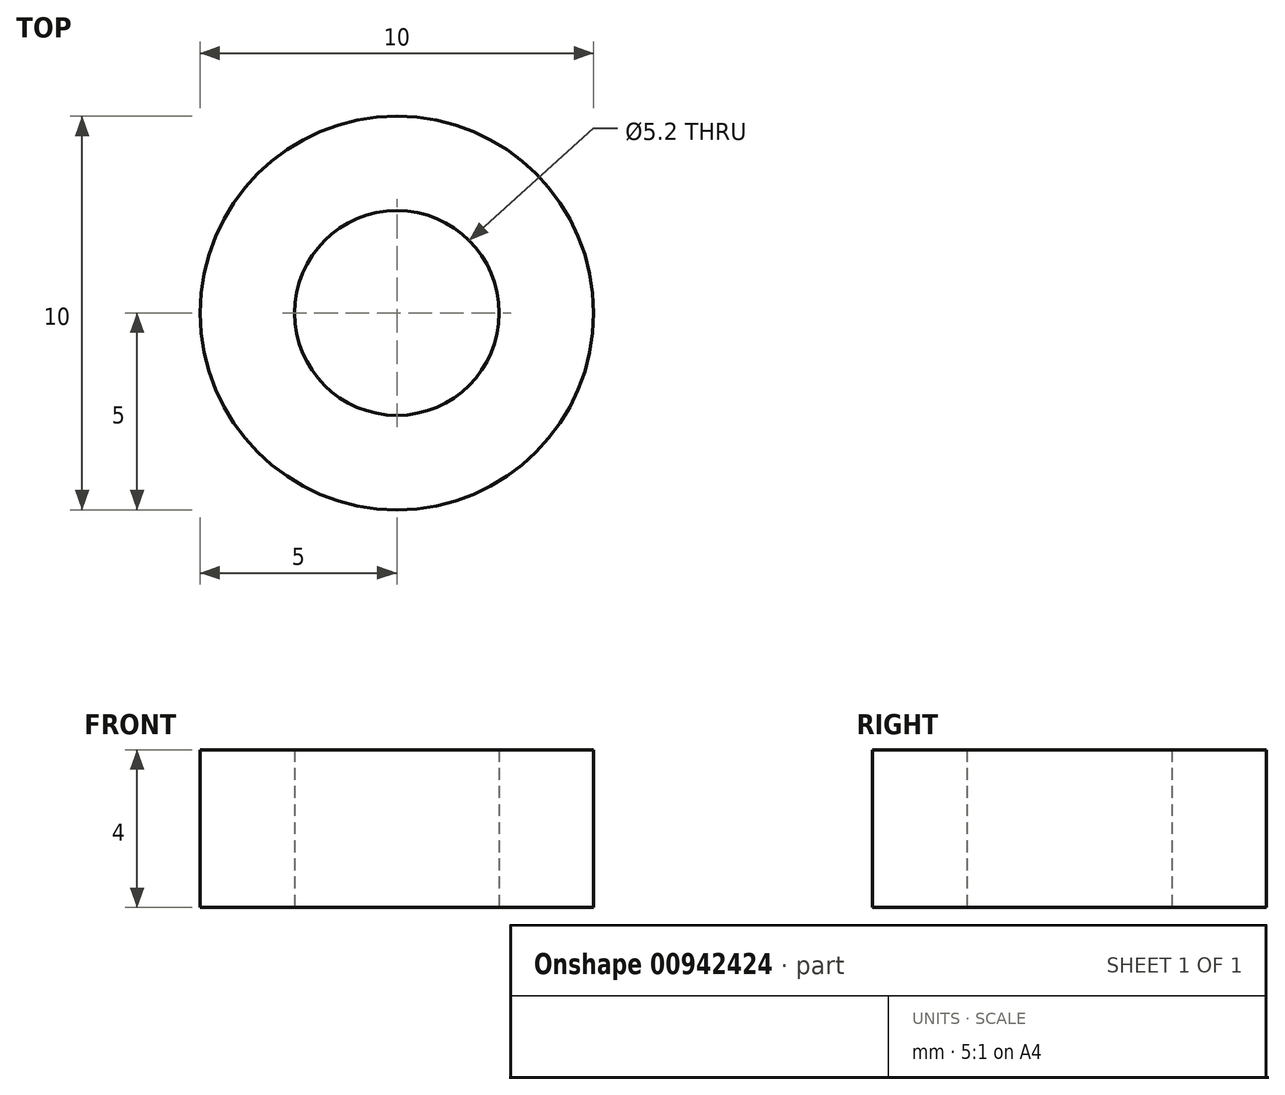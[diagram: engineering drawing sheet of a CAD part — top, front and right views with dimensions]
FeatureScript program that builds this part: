
annotation { "Feature Type Name" : "Feature", "Feature Type Description" : "" }
export const myFeature = defineFeature(function(context is Context, id is Id, definition is map)
    precondition{}
    {
        {
            var Q0;
            Q0=qCreatedBy(makeId("Front.planeOp"),FACE);
            var sketch = newSketch(context, id + "F0", { "sketchPlane" : qUnion([Q0])});
            skLineSegment(sketch, "E0", {"start": v(9.37, 10) * mm, "end": v(9.37, 25) * mm});
            skLineSegment(sketch, "E1", {"start": v(9.37, 25) * mm, "end": v(-30.63, 25) * mm});
            skLineSegment(sketch, "E2", {"start": v(-30.63, 25) * mm, "end": v(-30.63, -25) * mm});
            skLineSegment(sketch, "E3", {"start": v(9.37, -25) * mm, "end": v(9.37, 0) * mm});
            skLineSegment(sketch, "E4", {"start": v(-30.63, -25) * mm, "end": v(9.37, -25) * mm});
            skLineSegment(sketch, "E5", {"start": v(9.37, 10) * mm, "end": v(-10.63, 10) * mm});
            skLineSegment(sketch, "E6", {"start": v(-10.63, 10) * mm, "end": v(-10.63, 0) * mm});
            skLineSegment(sketch, "E7", {"start": v(-10.63, 0) * mm, "end": v(9.37, 0) * mm});
            skLineSegment(sketch, "E8.bottom", {"start": v(-4.1, -6) * mm, "end": v(4.1, -6) * mm});
            skLineSegment(sketch, "E8.top", {"start": v(-4.1, -9.2) * mm, "end": v(4.1, -9.2) * mm});
            skLineSegment(sketch, "E8.left", {"start": v(-4.1, -6) * mm, "end": v(-4.1, -9.2) * mm});
            skLineSegment(sketch, "E8.right", {"start": v(4.1, -6) * mm, "end": v(4.1, -9.2) * mm});
            skFitSpline(sketch, "E9", {"points": [v(-25, 25) * mm, v(-21.25, -15.4) * mm, v(9.37, -19.87) * mm], "startDerivative": vector(2.03, -83.34) * mm, "endDerivative": vector(87.72, 0.68) * mm});
            skSolve(sketch);
        }
        {
            var Q0;
            Q0=qSketchRegion(id+"F0",true);
            extrude(context, id + "F1", {"entities" : qUnion([Q0]), "depth" : 25 * mm, "offsetDistance" : 25 * mm});
        }
        {
            var Q0;
            Q0=makeQuery(id+"F1.opExtrude","SWEPT_FACE",FACE,{"disambiguationData":[OSD([sQuery(id+"F0.wireOp",EDGE,"E1")])]});
            var sketch = newSketch(context, id + "F2", { "sketchPlane" : qUnion([Q0])});
            skCircle(sketch, "E10", {"center": v(-17.63, -12.5) * mm, "radius": 3 * mm});
            skPoint(sketch, "E10.centerSnap0", {"position": v(-10.63, 0) * mm});
            skPoint(sketch, "E10.centerSnap1", {"position": v(-30.63, -12.5) * mm});
            skSolve(sketch);
        }
        {
            var Q0;
            Q0=makeQuery(id+"F2.imprint","IMPRINT",FACE,{"disambiguationData":[TD([[makeQuery(id+"F2.imprint","IMPRINT",EDGE,{"derivedFrom":sQuery(id+"F2.wireOp",EDGE,"E10")}),1.0]])]});
            extrude(context, id + "F3", {"entities" : qUnion([Q0]), "operationType" : NewBodyOperationType.REMOVE, "oppositeDirection" : true, "depth" : 56.7 * mm, "offsetDistance" : 25 * mm});
        }
        {
            var Q0;
            Q0=makeQuery(id+"F1.opExtrude","SWEPT_FACE",FACE,{"disambiguationData":[OSD([sQuery(id+"F0.wireOp",EDGE,"E4")])]});
            var sketch = newSketch(context, id + "F4", { "sketchPlane" : qUnion([Q0])});
            skLineSegment(sketch, "E11", {"start": v(23.4, 12.5) * mm, "end": v(-73.54, 12.5) * mm, "construction": true});
            skLineSegment(sketch, "E12.0", {"start": v(-10.63, 25) * mm, "end": v(-10.63, 0) * mm, "construction": true});
            skCircle(sketch, "E13", {"center": v(0, 12.5) * mm, "radius": 2.6 * mm});
            skSolve(sketch);
        }
        {
            var Q0;
            Q0=makeQuery(id+"F4.imprint","IMPRINT",FACE,{"disambiguationData":[TD([[makeQuery(id+"F4.imprint","IMPRINT",EDGE,{"derivedFrom":sQuery(id+"F4.wireOp",EDGE,"E13")}),1.0]])]});
            extrude(context, id + "F5", {"entities" : qUnion([Q0]), "operationType" : NewBodyOperationType.REMOVE, "oppositeDirection" : true, "depth" : 25 * mm, "offsetDistance" : 25 * mm});
        }
        {
            var Q0;
            Q0=makeQuery(id+"F1.opExtrude","SWEPT_FACE",FACE,{"disambiguationData":[OSD([sQuery(id+"F0.wireOp",EDGE,"E7")])]});
            var sketch = newSketch(context, id + "F6", { "sketchPlane" : qUnion([Q0])});
            skCircle(sketch, "E14", {"center": v(0, -12.5) * mm, "radius": 7.5 * mm});
            skSolve(sketch);
        }
        {
            var Q0;
            Q0=makeQuery(id+"F6.imprint","IMPRINT",FACE,{"disambiguationData":[TD([[makeQuery(id+"F6.imprint","IMPRINT",EDGE,{"derivedFrom":sQuery(id+"F6.wireOp",EDGE,"E14")}),1.0]])]});
            extrude(context, id + "F7", {"entities" : qUnion([Q0]), "operationType" : NewBodyOperationType.REMOVE, "oppositeDirection" : true, "depth" : 5 * mm, "offsetDistance" : 25 * mm});
        }
        {
            var Q0;
            Q0=makeQuery(id+"F1.opExtrude","SWEPT_FACE",FACE,{"disambiguationData":[OSD([sQuery(id+"F0.wireOp",EDGE,"E4")])]});
            var sketch = newSketch(context, id + "F8", { "sketchPlane" : qUnion([Q0])});
            skSolve(sketch);
        }
        {
            var Q0;
            {var subQ0=sQuery(id+"F0.wireOp",EDGE,"E4");Q0=makeQuery(id+"F8.imprint","IMPRINT",FACE,{"disambiguationData":[TD([[makeQuery(id+"F8.imprint","IMPRINT",EDGE,{"derivedFrom":makeQuery(id+"F1.opExtrude","CAP_EDGE",EDGE,{"disambiguationData":[OSD([subQ0])],"isStart":true})}),1.0]])]});}
            var sketch = newSketch(context, id + "F9", { "sketchPlane" : qUnion([Q0])});
            skCircle(sketch, "E15.0", {"center": v(-17.63, 12.5) * mm, "radius": 3 * mm, "construction": true});
            skCircle(sketch, "E16.cCircle", {"center": v(-17.63, 12.5) * mm, "radius": 4 * mm, "construction": true});
            skLineSegment(sketch, "E16.0", {"start": v(-15.32, 8.5) * mm, "end": v(-19.94, 8.5) * mm});
            skLineSegment(sketch, "E16.1", {"start": v(-19.94, 8.5) * mm, "end": v(-22.25, 12.5) * mm});
            skLineSegment(sketch, "E16.2", {"start": v(-22.25, 12.5) * mm, "end": v(-19.94, 16.5) * mm});
            skLineSegment(sketch, "E16.3", {"start": v(-19.94, 16.5) * mm, "end": v(-15.32, 16.5) * mm});
            skLineSegment(sketch, "E16.4", {"start": v(-15.32, 16.5) * mm, "end": v(-13.02, 12.5) * mm});
            skLineSegment(sketch, "E16.5", {"start": v(-13.02, 12.5) * mm, "end": v(-15.32, 8.5) * mm});
            skPoint(sketch, "E16.0.midPoint", {"position": v(-17.63, 8.5) * mm});
            skSolve(sketch);
        }
        {
            var Q0;
            Q0=makeQuery(id+"F9.imprint","IMPRINT",FACE,{"disambiguationData":[TD([[makeQuery(id+"F9.imprint","IMPRINT",EDGE,{"derivedFrom":sQuery(id+"F9.wireOp",EDGE,"E16.0")}),-1.0]])]});
            extrude(context, id + "F10", {"entities" : qUnion([Q0]), "operationType" : NewBodyOperationType.REMOVE, "oppositeDirection" : true, "depth" : 13 * mm, "offsetDistance" : 25 * mm});
        }
        {
            var Q0;
            Q0=makeQuery(id+"F1.opExtrude","CAP_FACE",FACE,{"disambiguationData":[OSD([sQuery(id+"F0.wireOp",EDGE,"E0"),sQuery(id+"F0.wireOp",EDGE,"E1"),sQuery(id+"F0.wireOp",EDGE,"E2"),sQuery(id+"F0.wireOp",EDGE,"E3"),sQuery(id+"F0.wireOp",EDGE,"E4"),sQuery(id+"F0.wireOp",EDGE,"E5"),sQuery(id+"F0.wireOp",EDGE,"E6"),sQuery(id+"F0.wireOp",EDGE,"E7"),sQuery(id+"F0.wireOp",EDGE,"E8.bottom"),sQuery(id+"F0.wireOp",EDGE,"E8.top"),sQuery(id+"F0.wireOp",EDGE,"E8.left"),sQuery(id+"F0.wireOp",EDGE,"E8.right")])],"isStart":false});
            var sketch = newSketch(context, id + "F11", { "sketchPlane" : qUnion([Q0])});
            skFitSpline(sketch, "E17", {"points": [v(-30.63, 25) * mm, v(-22.39, -16.37) * mm, v(-4.24, -25) * mm, v(-3.87, -25) * mm], "startDerivative": vector(-1.47, -87.32) * mm, "endDerivative": vector(3.99, 0.77) * mm});
            skSolve(sketch);
        }
        {
            var Q0;
            {var subQ0=sQuery(id+"F11.wireOp",EDGE,"E17");var subQ1=makeQuery(id+"F1.opExtrude","CAP_EDGE",EDGE,{"disambiguationData":[OSD([sQuery(id+"F0.wireOp",EDGE,"E2")])],"isStart":false});var subQ2=makeQuery(id+"F11.imprint","INTERSECT",VERTEX,{"derivedFrom":[subQ1,subQ0]});Q0=makeQuery(id+"F11.imprint","IMPRINT",FACE,{"disambiguationData":[TD([[makeQuery(id+"F11.imprint","IMPRINT",EDGE,{"disambiguationData":[TD([[subQ2,-1.0]])],"derivedFrom":subQ0}),-1.0]])]});}
            extrude(context, id + "F12", {"entities" : qUnion([Q0]), "operationType" : NewBodyOperationType.REMOVE, "oppositeDirection" : true, "depth" : 29.7 * mm, "offsetDistance" : 25 * mm});
        }
        {
            var Q0;
            Q0=makeQuery(id+"F1.opExtrude","CAP_EDGE",EDGE,{"disambiguationData":[OSD([sQuery(id+"F0.wireOp",EDGE,"E4")])],"isStart":false});
            var Q1;
            Q1=makeQuery(id+"F1.opExtrude","CAP_EDGE",EDGE,{"disambiguationData":[OSD([sQuery(id+"F0.wireOp",EDGE,"E4")])],"isStart":true});
            var Q2;
            Q2=makeQuery(id+"F12.boolean.opBoolean","COPY",EDGE,{"derivedFrom":makeQuery(id+"F12.opExtrude","CAP_EDGE",EDGE,{"disambiguationData":[OSD([sQuery(id+"F11.wireOp",EDGE,"E17")])],"isStart":true})});
            var Q3;
            Q3=makeQuery(id+"F12.boolean.opBoolean","INTERSECT",EDGE,{"derivedFrom":[makeQuery(id+"F1.opExtrude","CAP_FACE",FACE,{"disambiguationData":[OSD([sQuery(id+"F0.wireOp",EDGE,"E0"),sQuery(id+"F0.wireOp",EDGE,"E1"),sQuery(id+"F0.wireOp",EDGE,"E2"),sQuery(id+"F0.wireOp",EDGE,"E3"),sQuery(id+"F0.wireOp",EDGE,"E4"),sQuery(id+"F0.wireOp",EDGE,"E5"),sQuery(id+"F0.wireOp",EDGE,"E6"),sQuery(id+"F0.wireOp",EDGE,"E7"),sQuery(id+"F0.wireOp",EDGE,"E8.bottom"),sQuery(id+"F0.wireOp",EDGE,"E8.top"),sQuery(id+"F0.wireOp",EDGE,"E8.left"),sQuery(id+"F0.wireOp",EDGE,"E8.right")])],"isStart":true}),makeQuery(id+"F12.opExtrude","SWEPT_FACE",FACE,{"disambiguationData":[OSD([sQuery(id+"F11.wireOp",EDGE,"E17")])]})]});
            fillet(context, id + "F13", {"entities" : qUnion([Q0, Q1, Q2, Q3]), "radius" : 2 * mm, "tangentPropagation" : true, "allowEdgeOverflow" : false});
        }
        {
            var Q0;
            Q0=makeQuery(id+"F1.opExtrude","SWEPT_EDGE",EDGE,{"disambiguationData":[OSD([sQuery(id+"F0.wireOp",EDGE,"E1"),sQuery(id+"F0.wireOp",EDGE,"E2")])]});
            fillet(context, id + "F14", {"entities" : qUnion([Q0]), "radius" : 8 * mm, "tangentPropagation" : true, "allowEdgeOverflow" : false});
        }
        {
            var Q0;
            Q0=makeQuery(id+"F7.boolean.opBoolean","COPY",FACE,{"derivedFrom":makeQuery(id+"F7.opExtrude","CAP_FACE",FACE,{"disambiguationData":[OSD([sQuery(id+"F4.wireOp",EDGE,"E13"),sQuery(id+"F6.wireOp",EDGE,"E14")])],"isStart":false})});
            var sketch = newSketch(context, id + "F15", { "sketchPlane" : qUnion([Q0])});
            skCircle(sketch, "E18", {"center": v(0, -12.5) * mm, "radius": 5 * mm});
            skSolve(sketch);
        }
        {
            var Q0;
            Q0=makeQuery(id+"F15.imprint","IMPRINT",FACE,{"disambiguationData":[TD([[makeQuery(id+"F15.imprint","IMPRINT",EDGE,{"derivedFrom":makeQuery(id+"F7.boolean.opBoolean","COPY",EDGE,{"derivedFrom":makeQuery(id+"F7.opExtrude","CAP_EDGE",EDGE,{"disambiguationData":[OSD([sQuery(id+"F4.wireOp",EDGE,"E13")])],"isStart":false})})}),-1.0]])]});
            var Q1;
            Q1=makeQuery(id+"F15.imprint","IMPRINT",FACE,{"disambiguationData":[TD([[makeQuery(id+"F15.imprint","IMPRINT",EDGE,{"derivedFrom":sQuery(id+"F15.wireOp",EDGE,"E18")}),1.0]])]});
            extrude(context, id + "F16", {"entities" : qUnion([Q0, Q1]), "depth" : 4 * mm, "offsetDistance" : 25 * mm});
        }
        {
            var Q0;
            Q0=makeQuery(id+"F1.opExtrude","SWEPT_BODY",BODY,{"disambiguationData":[OSD([sQuery(id+"F0.wireOp",EDGE,"E0"),sQuery(id+"F0.wireOp",EDGE,"E1"),sQuery(id+"F0.wireOp",EDGE,"E2"),sQuery(id+"F0.wireOp",EDGE,"E3"),sQuery(id+"F0.wireOp",EDGE,"E4"),sQuery(id+"F0.wireOp",EDGE,"E5"),sQuery(id+"F0.wireOp",EDGE,"E6"),sQuery(id+"F0.wireOp",EDGE,"E7"),sQuery(id+"F0.wireOp",EDGE,"E8.bottom"),sQuery(id+"F0.wireOp",EDGE,"E8.top"),sQuery(id+"F0.wireOp",EDGE,"E8.left"),sQuery(id+"F0.wireOp",EDGE,"E8.right")])]});
            deleteBodies(context, id + "F17", {"entities" : qUnion([Q0])});
        }
    });
